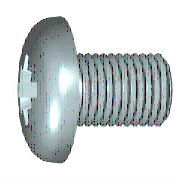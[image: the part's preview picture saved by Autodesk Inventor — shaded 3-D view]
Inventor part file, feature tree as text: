
AUTODESK INVENTOR PART (.ipt)
format: ipt  version: 2022 (Build 260153000, 153)  size: 344,064 bytes
history: native  units: mm (DEFAULTED — no unit token found)
features: other x2, plane x2, extrude x2
ambient origin geometry x7: Origin, YZ Plane, XZ Plane, X Axis, Y Axis, Z Axis, Center Point
bodies: Solid1 (feature_tree)
feature tree (6):
  other  "Базовый элемент"
  plane  "Work Plane1"
  extrude  "Паз"  Depth=6.0mm
  other  "Вырез"
  extrude  "Прорезь крестообразная"  Depth=3.6mm
  plane  "Work Plane3"
